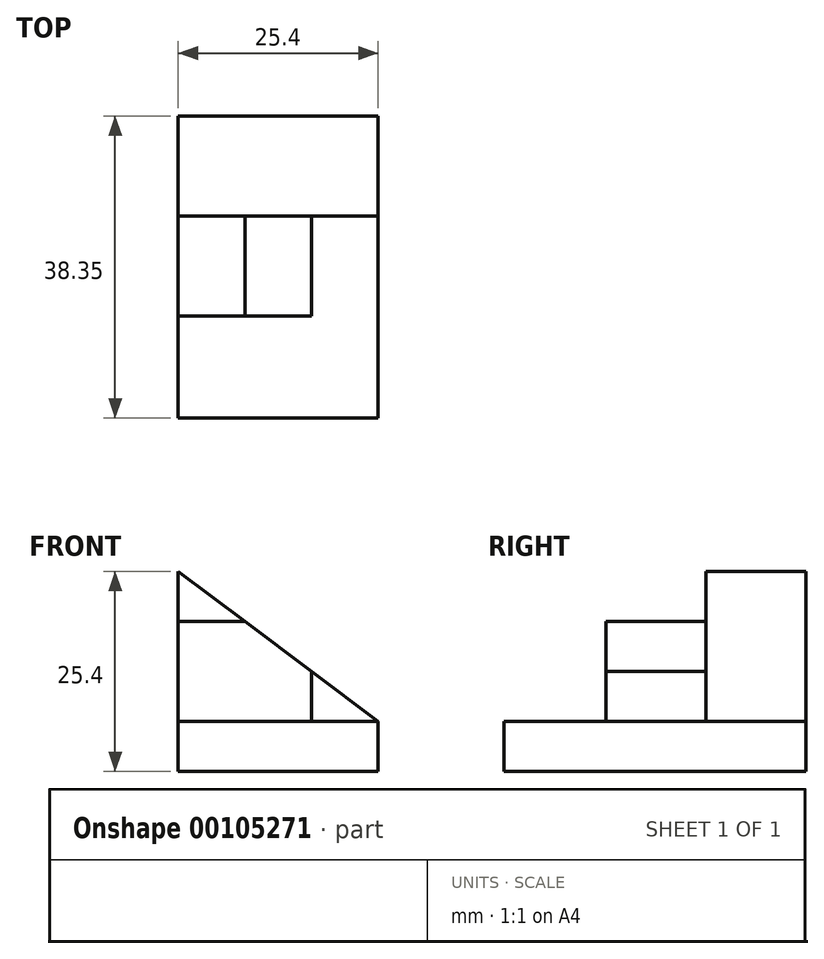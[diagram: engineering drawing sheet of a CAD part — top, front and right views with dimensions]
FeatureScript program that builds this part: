
annotation { "Feature Type Name" : "Feature", "Feature Type Description" : "" }
export const myFeature = defineFeature(function(context is Context, id is Id, definition is map)
    precondition{}
    {
        {
            var Q0;
            Q0=qCreatedBy(makeId("Front.planeOp"),FACE);
            var sketch = newSketch(context, id + "F0", { "sketchPlane" : qUnion([Q0])});
            skLineSegment(sketch, "E0.bottom", {"start": v(0, 0) * mm, "end": v(25.4, 0) * mm});
            skLineSegment(sketch, "E0.top", {"start": v(0, 6.35) * mm, "end": v(25.4, 6.35) * mm});
            skLineSegment(sketch, "E0.left", {"start": v(0, 0) * mm, "end": v(0, 6.35) * mm});
            skLineSegment(sketch, "E0.right", {"start": v(25.4, 0) * mm, "end": v(25.4, 6.35) * mm});
            skSolve(sketch);
        }
        {
            var Q0;
            Q0=makeQuery(id+"F0.imprint","IMPRINT",FACE,{"disambiguationData":[TD([[makeQuery(id+"F0.imprint","IMPRINT",EDGE,{"derivedFrom":sQuery(id+"F0.wireOp",EDGE,"E0.bottom")}),1.0]])]});
            extrude(context, id + "F1", {"entities" : qUnion([Q0]), "oppositeDirection" : true, "depth" : 38.35 * mm});
        }
        {
            var Q0;
            Q0=makeQuery(id+"F1.opExtrude","CAP_FACE",FACE,{"disambiguationData":[OSD([sQuery(id+"F0.wireOp",EDGE,"E0.bottom"),sQuery(id+"F0.wireOp",EDGE,"E0.top"),sQuery(id+"F0.wireOp",EDGE,"E0.left"),sQuery(id+"F0.wireOp",EDGE,"E0.right")])],"isStart":false});
            var sketch = newSketch(context, id + "F2", { "sketchPlane" : qUnion([Q0])});
            skLineSegment(sketch, "E1.bottom", {"start": v(0, 6.35) * mm, "end": v(-25.4, 6.35) * mm});
            skLineSegment(sketch, "E1.left", {"start": v(0, 6.35) * mm, "end": v(0, 25.4) * mm});
            skLineSegment(sketch, "E2", {"start": v(-25.4, 6.35) * mm, "end": v(0, 25.4) * mm});
            skSolve(sketch);
        }
        {
            var Q0;
            Q0=makeQuery(id+"F2.imprint","IMPRINT",FACE,{"disambiguationData":[TD([[makeQuery(id+"F2.imprint","IMPRINT",EDGE,{"derivedFrom":sQuery(id+"F2.wireOp",EDGE,"E1.bottom")}),-1.0]])]});
            extrude(context, id + "F3", {"entities" : qUnion([Q0]), "operationType" : NewBodyOperationType.ADD, "oppositeDirection" : true, "depth" : 12.7 * mm});
        }
        {
            var Q0;
            Q0=makeQuery(id+"F3.opExtrude","CAP_FACE",FACE,{"disambiguationData":[OSD([sQuery(id+"F2.wireOp",EDGE,"E1.bottom"),sQuery(id+"F2.wireOp",EDGE,"E1.left"),sQuery(id+"F2.wireOp",EDGE,"E2")])],"isStart":false});
            var sketch = newSketch(context, id + "F4", { "sketchPlane" : qUnion([Q0])});
            skLineSegment(sketch, "E3", {"start": v(16.93, 6.35) * mm, "end": v(16.93, 12.7) * mm});
            skLineSegment(sketch, "E4", {"start": v(0, 6.35) * mm, "end": v(16.93, 6.35) * mm});
            skLineSegment(sketch, "E5", {"start": v(0, 19.05) * mm, "end": v(8.47, 19.05) * mm});
            skSolve(sketch);
        }
        {
            var Q0;
            {var subQ1=sQuery(id+"F4.wireOp",EDGE,"E3");Q0=makeQuery(id+"F4.imprint","IMPRINT",FACE,{"disambiguationData":[TD([[makeQuery(id+"F4.imprint","IMPRINT",EDGE,{"derivedFrom":subQ1}),1.0]])]});}
            extrude(context, id + "F5", {"entities" : qUnion([Q0]), "operationType" : NewBodyOperationType.ADD, "depth" : 12.7 * mm});
        }
        {
            var Q0;
            Q0=makeQuery(id+"F4.imprint","IMPRINT",FACE,{"disambiguationData":[TD([[makeQuery(id+"F4.imprint","IMPRINT",EDGE,{"derivedFrom":sQuery(id+"F4.wireOp",EDGE,"E3")}),1.0]])]});
            extrude(context, id + "F6", {"entities" : qUnion([Q0]), "depth" : 12.7 * mm});
        }
    });
